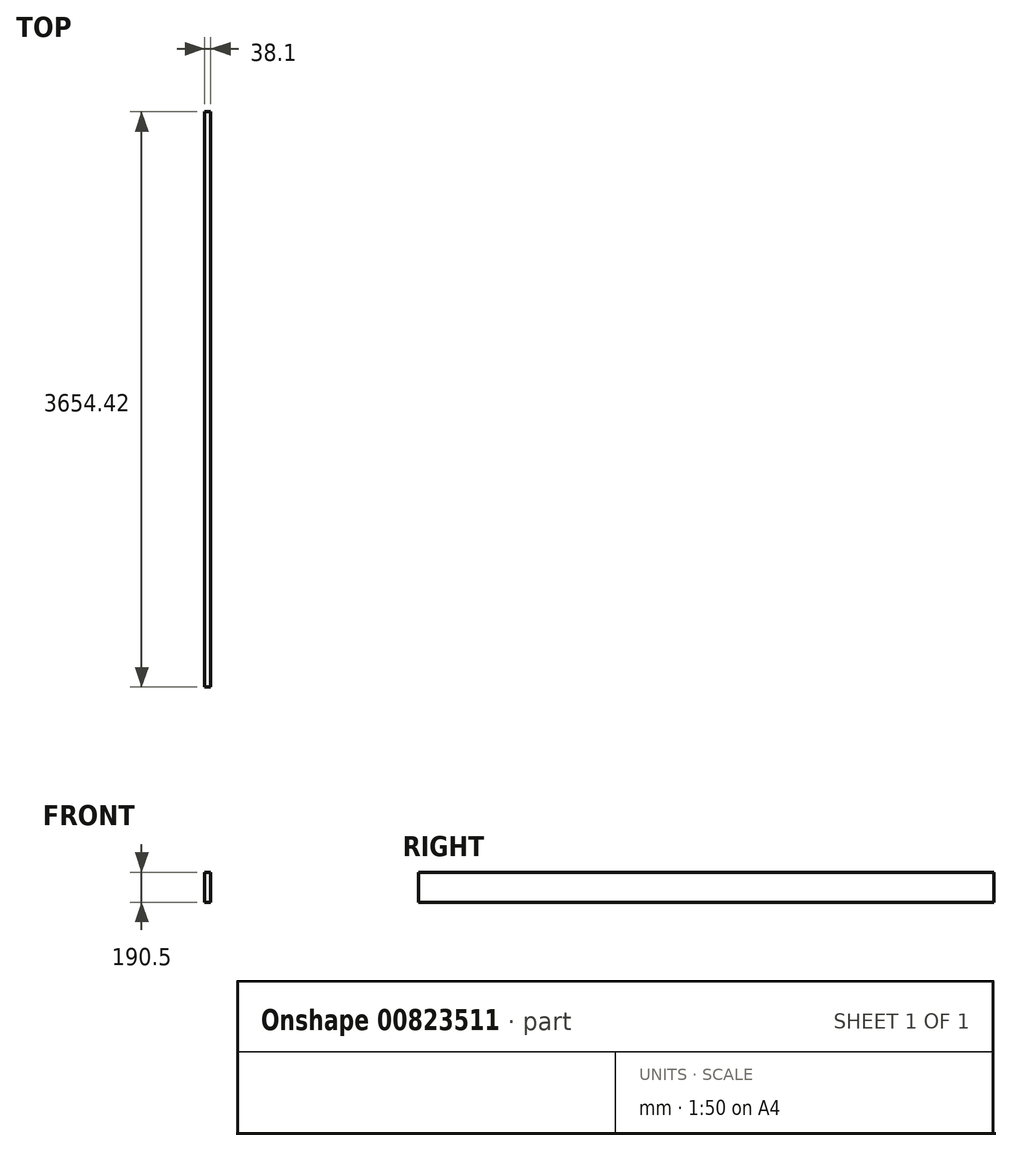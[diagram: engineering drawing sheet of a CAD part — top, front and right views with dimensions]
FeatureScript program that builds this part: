
annotation { "Feature Type Name" : "Feature", "Feature Type Description" : "" }
export const myFeature = defineFeature(function(context is Context, id is Id, definition is map)
    precondition{}
    {
        {
            var Q0;
            Q0=qCreatedBy(makeId("Front.planeOp"),FACE);
            var sketch = newSketch(context, id + "F0", { "sketchPlane" : qUnion([Q0])});
            skLineSegment(sketch, "E0.bottom", {"start": v(0, 0) * mm, "end": v(38.1, 0) * mm});
            skLineSegment(sketch, "E0.top", {"start": v(0, 190.5) * mm, "end": v(38.1, 190.5) * mm});
            skLineSegment(sketch, "E0.left", {"start": v(0, 0) * mm, "end": v(0, 190.5) * mm});
            skLineSegment(sketch, "E0.right", {"start": v(38.1, 0) * mm, "end": v(38.1, 190.5) * mm});
            skSolve(sketch);
        }
        {
            var Q0;
            Q0=qSketchRegion(id+"F0",true);
            extrude(context, id + "F1", {"entities" : qUnion([Q0]), "depth" : 3654.42 * mm, "offsetDistance" : 25.4 * mm});
        }
    });
